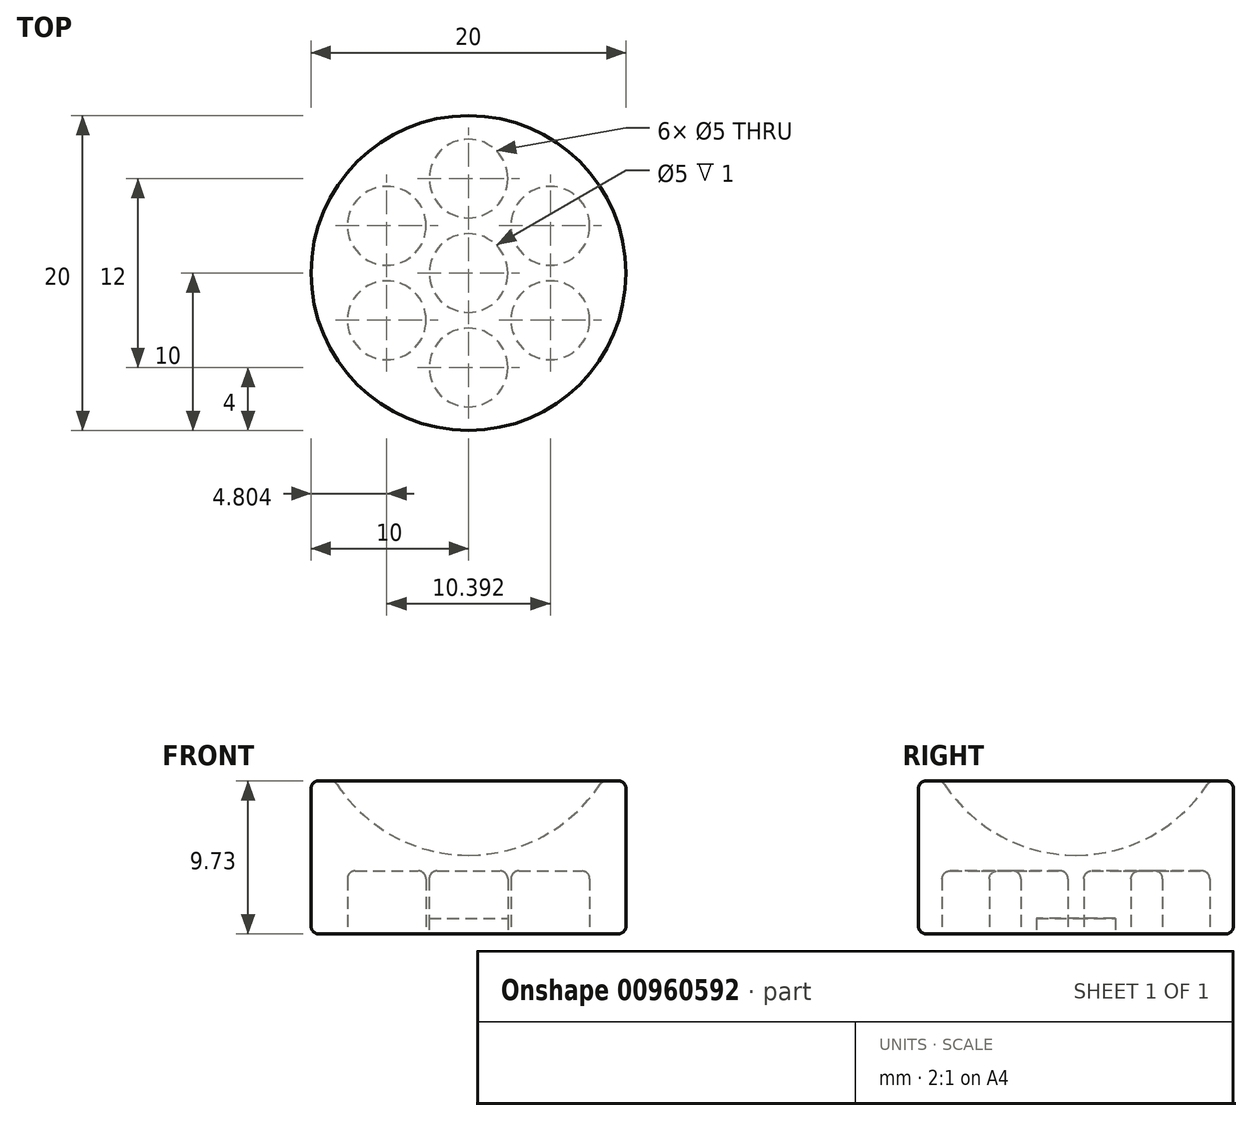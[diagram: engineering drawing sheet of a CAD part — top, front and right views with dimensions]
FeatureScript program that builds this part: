
annotation { "Feature Type Name" : "Feature", "Feature Type Description" : "" }
export const myFeature = defineFeature(function(context is Context, id is Id, definition is map)
    precondition{}
    {
        {
            var Q0;
            Q0=qCreatedBy(makeId("Front.planeOp"),FACE);
            var sketch = newSketch(context, id + "F0", { "sketchPlane" : qUnion([Q0])});
            skCircle(sketch, "E0", {"center": v(0, 0) * mm, "radius": 10 * mm});
            skLineSegment(sketch, "E1", {"start": v(8.5, -5.27) * mm, "end": v(10, -5.27) * mm});
            skLineSegment(sketch, "E2", {"start": v(10, -5.27) * mm, "end": v(10, -15) * mm});
            skLineSegment(sketch, "E3", {"start": v(10, -15) * mm, "end": v(0, -15) * mm});
            skLineSegment(sketch, "E4", {"start": v(0, -15) * mm, "end": v(0, -10) * mm});
            skSolve(sketch);
        }
        {
            var Q0;
            {var subQ0=sQuery(id+"F0.wireOp",EDGE,"E1");Q0=makeQuery(id+"F0.imprint","IMPRINT",FACE,{"disambiguationData":[TD([[makeQuery(id+"F0.imprint","IMPRINT",EDGE,{"derivedFrom":subQ0}),-1.0]])]});}
            var Q1;
            Q1=sQuery(id+"F0.wireOp",EDGE,"E4");
            revolve(context, id + "F1", {"surfaceOperationType" : NewSurfaceOperationType.NEW, "entities" : qUnion([Q0]), "axis" : qUnion([Q1]), "revolveType" : RevolveType.FULL});
        }
        {
            var Q0;
            Q0=makeQuery(id+"F1.opRevolve","SWEPT_FACE",FACE,{"disambiguationData":[OSD([sQuery(id+"F0.wireOp",EDGE,"E3")])]});
            var sketch = newSketch(context, id + "F2", { "sketchPlane" : qUnion([Q0])});
            skCircle(sketch, "E5", {"center": v(0, 0) * mm, "radius": 2.5 * mm});
            skSolve(sketch);
        }
        {
            var Q0;
            Q0=makeQuery(id+"F2.imprint","IMPRINT",FACE,{"disambiguationData":[TD([[makeQuery(id+"F2.imprint","IMPRINT",EDGE,{"derivedFrom":sQuery(id+"F2.wireOp",EDGE,"E5")}),1.0]])]});
            extrude(context, id + "F3", {"entities" : qUnion([Q0]), "operationType" : NewBodyOperationType.REMOVE, "oppositeDirection" : true, "depth" : 1 * mm, "offsetDistance" : 25 * mm});
        }
        {
            var Q0;
            Q0=makeQuery(id+"F1.opRevolve","SWEPT_FACE",FACE,{"disambiguationData":[OSD([sQuery(id+"F0.wireOp",EDGE,"E3")])]});
            var sketch = newSketch(context, id + "F4", { "sketchPlane" : qUnion([Q0])});
            skCircle(sketch, "E6", {"center": v(0, 6) * mm, "radius": 2.5 * mm});
            skCircle(sketch, "E7.1.0", {"center": v(-5.2, 3) * mm, "radius": 2.5 * mm});
            skCircle(sketch, "E7.2.0", {"center": v(-5.2, -3) * mm, "radius": 2.5 * mm});
            skCircle(sketch, "E7.3.0", {"center": v(0, -6) * mm, "radius": 2.5 * mm});
            skCircle(sketch, "E7.4.0", {"center": v(5.2, -3) * mm, "radius": 2.5 * mm});
            skCircle(sketch, "E7.5.0", {"center": v(5.2, 3) * mm, "radius": 2.5 * mm});
            skPoint(sketch, "E7.center", {"position": v(0, 0) * mm});
            skSolve(sketch);
        }
        {
            var Q0;
            Q0=makeQuery(id+"F4.imprint","IMPRINT",FACE,{"disambiguationData":[TD([[makeQuery(id+"F4.imprint","IMPRINT",EDGE,{"derivedFrom":sQuery(id+"F4.wireOp",EDGE,"E7.1.0")}),1.0]])]});
            var Q1;
            Q1=makeQuery(id+"F4.imprint","IMPRINT",FACE,{"disambiguationData":[TD([[makeQuery(id+"F4.imprint","IMPRINT",EDGE,{"derivedFrom":sQuery(id+"F4.wireOp",EDGE,"E6")}),1.0]])]});
            var Q2;
            Q2=makeQuery(id+"F4.imprint","IMPRINT",FACE,{"disambiguationData":[TD([[makeQuery(id+"F4.imprint","IMPRINT",EDGE,{"derivedFrom":sQuery(id+"F4.wireOp",EDGE,"E7.5.0")}),1.0]])]});
            var Q3;
            Q3=makeQuery(id+"F4.imprint","IMPRINT",FACE,{"disambiguationData":[TD([[makeQuery(id+"F4.imprint","IMPRINT",EDGE,{"derivedFrom":sQuery(id+"F4.wireOp",EDGE,"E7.4.0")}),1.0]])]});
            var Q4;
            Q4=makeQuery(id+"F4.imprint","IMPRINT",FACE,{"disambiguationData":[TD([[makeQuery(id+"F4.imprint","IMPRINT",EDGE,{"derivedFrom":sQuery(id+"F4.wireOp",EDGE,"E7.3.0")}),1.0]])]});
            var Q5;
            Q5=makeQuery(id+"F4.imprint","IMPRINT",FACE,{"disambiguationData":[TD([[makeQuery(id+"F4.imprint","IMPRINT",EDGE,{"derivedFrom":sQuery(id+"F4.wireOp",EDGE,"E7.2.0")}),1.0]])]});
            extrude(context, id + "F5", {"entities" : qUnion([Q0, Q1, Q2, Q3, Q4, Q5]), "operationType" : NewBodyOperationType.REMOVE, "oppositeDirection" : true, "depth" : 4 * mm, "offsetDistance" : 25 * mm});
        }
        {
            var Q0;
            Q0=makeQuery(id+"F5.boolean.opBoolean","COPY",EDGE,{"derivedFrom":makeQuery(id+"F5.opExtrude","CAP_EDGE",EDGE,{"disambiguationData":[OSD([sQuery(id+"F4.wireOp",EDGE,"E7.4.0")])],"isStart":true})});
            var Q1;
            Q1=makeQuery(id+"F5.boolean.opBoolean","COPY",EDGE,{"derivedFrom":makeQuery(id+"F5.opExtrude","CAP_EDGE",EDGE,{"disambiguationData":[OSD([sQuery(id+"F4.wireOp",EDGE,"E7.3.0")])],"isStart":true})});
            var Q2;
            Q2=makeQuery(id+"F5.boolean.opBoolean","COPY",EDGE,{"derivedFrom":makeQuery(id+"F5.opExtrude","CAP_EDGE",EDGE,{"disambiguationData":[OSD([sQuery(id+"F4.wireOp",EDGE,"E7.2.0")])],"isStart":true})});
            var Q3;
            Q3=makeQuery(id+"F5.boolean.opBoolean","COPY",EDGE,{"derivedFrom":makeQuery(id+"F5.opExtrude","CAP_EDGE",EDGE,{"disambiguationData":[OSD([sQuery(id+"F4.wireOp",EDGE,"E7.1.0")])],"isStart":true})});
            var Q4;
            Q4=makeQuery(id+"F5.boolean.opBoolean","COPY",EDGE,{"derivedFrom":makeQuery(id+"F5.opExtrude","CAP_EDGE",EDGE,{"disambiguationData":[OSD([sQuery(id+"F4.wireOp",EDGE,"E6")])],"isStart":true})});
            var Q5;
            Q5=makeQuery(id+"F5.boolean.opBoolean","COPY",EDGE,{"derivedFrom":makeQuery(id+"F5.opExtrude","CAP_EDGE",EDGE,{"disambiguationData":[OSD([sQuery(id+"F4.wireOp",EDGE,"E7.5.0")])],"isStart":true})});
            var Q6;
            Q6=makeQuery(id+"F5.boolean.opBoolean","COPY",EDGE,{"derivedFrom":makeQuery(id+"F5.opExtrude","CAP_EDGE",EDGE,{"disambiguationData":[OSD([sQuery(id+"F4.wireOp",EDGE,"E7.4.0")])],"isStart":false})});
            var Q7;
            Q7=makeQuery(id+"F5.boolean.opBoolean","COPY",EDGE,{"derivedFrom":makeQuery(id+"F5.opExtrude","CAP_EDGE",EDGE,{"disambiguationData":[OSD([sQuery(id+"F4.wireOp",EDGE,"E7.3.0")])],"isStart":false})});
            var Q8;
            Q8=makeQuery(id+"F5.boolean.opBoolean","COPY",EDGE,{"derivedFrom":makeQuery(id+"F5.opExtrude","CAP_EDGE",EDGE,{"disambiguationData":[OSD([sQuery(id+"F4.wireOp",EDGE,"E7.2.0")])],"isStart":false})});
            var Q9;
            Q9=makeQuery(id+"F5.boolean.opBoolean","COPY",EDGE,{"derivedFrom":makeQuery(id+"F5.opExtrude","CAP_EDGE",EDGE,{"disambiguationData":[OSD([sQuery(id+"F4.wireOp",EDGE,"E7.1.0")])],"isStart":false})});
            var Q10;
            Q10=makeQuery(id+"F5.boolean.opBoolean","COPY",EDGE,{"derivedFrom":makeQuery(id+"F5.opExtrude","CAP_EDGE",EDGE,{"disambiguationData":[OSD([sQuery(id+"F4.wireOp",EDGE,"E6")])],"isStart":false})});
            var Q11;
            Q11=makeQuery(id+"F5.boolean.opBoolean","COPY",EDGE,{"derivedFrom":makeQuery(id+"F5.opExtrude","CAP_EDGE",EDGE,{"disambiguationData":[OSD([sQuery(id+"F4.wireOp",EDGE,"E7.5.0")])],"isStart":false})});
            fillet(context, id + "F6", {"entities" : qUnion([Q0, Q1, Q2, Q3, Q4, Q5, Q6, Q7, Q8, Q9, Q10, Q11]), "radius" : .5 * mm, "tangentPropagation" : true, "allowEdgeOverflow" : false});
        }
        {
            var Q0;
            Q0=makeQuery(id+"F1.opRevolve","SWEPT_EDGE",EDGE,{"disambiguationData":[OSD([sQuery(id+"F0.wireOp",EDGE,"E2"),sQuery(id+"F0.wireOp",EDGE,"E3")])]});
            var Q1;
            Q1=makeQuery(id+"F1.opRevolve","SWEPT_EDGE",EDGE,{"disambiguationData":[OSD([sQuery(id+"F0.wireOp",EDGE,"E1"),sQuery(id+"F0.wireOp",EDGE,"E2")])]});
            var Q2;
            Q2=makeQuery(id+"F1.opRevolve","SWEPT_EDGE",EDGE,{"disambiguationData":[OSD([sQuery(id+"F0.wireOp",EDGE,"E0"),sQuery(id+"F0.wireOp",EDGE,"E1")])]});
            fillet(context, id + "F7", {"entities" : qUnion([Q0, Q1, Q2]), "radius" : .5 * mm, "tangentPropagation" : true, "allowEdgeOverflow" : false});
        }
    });
